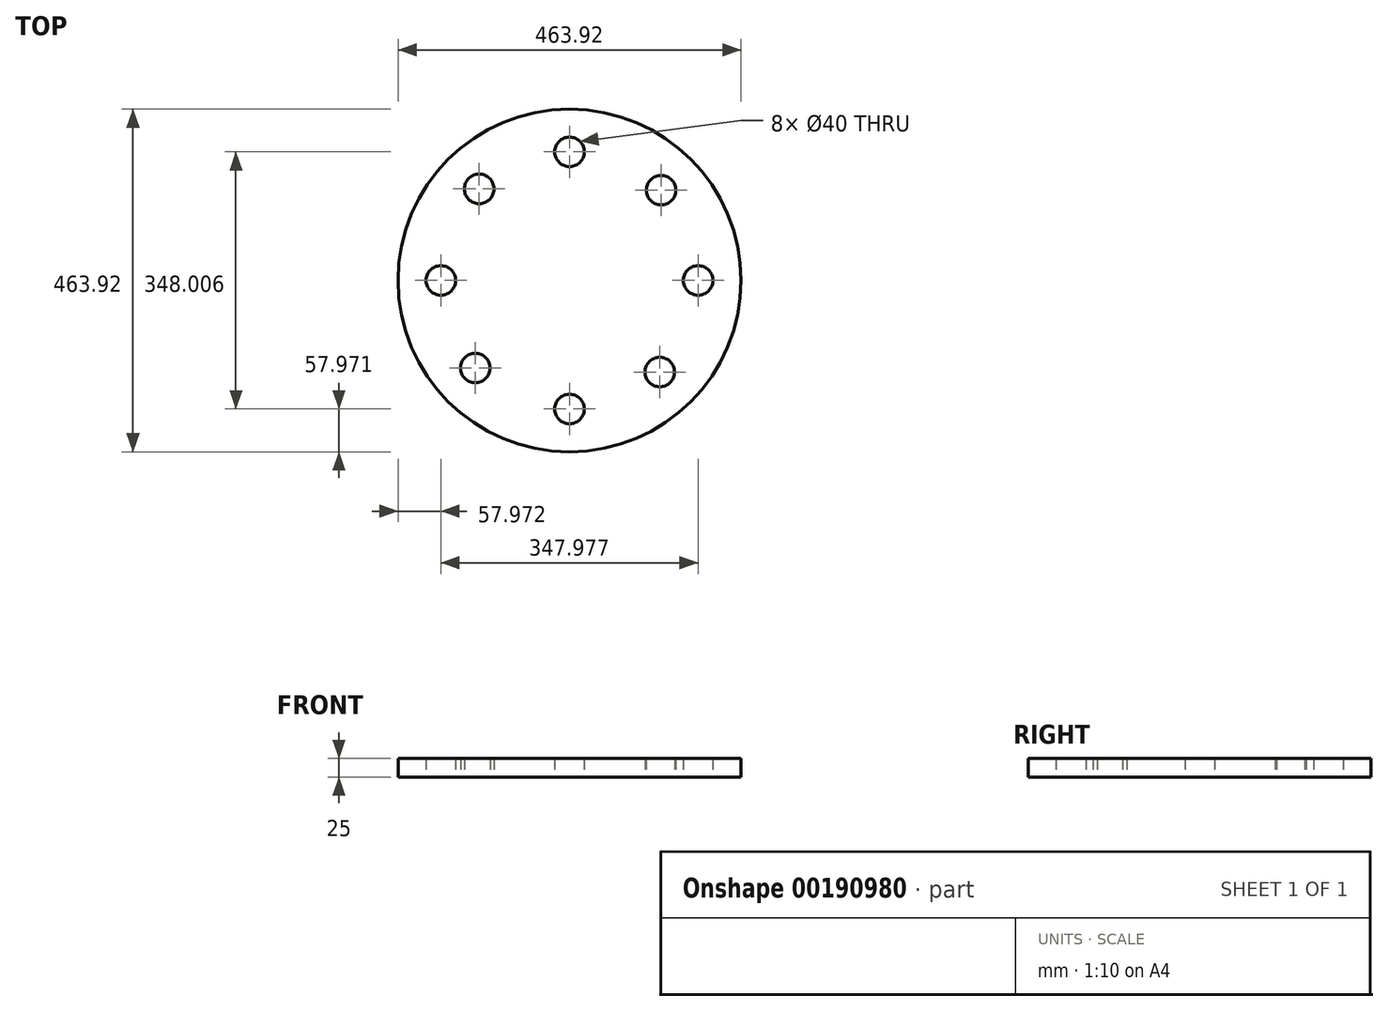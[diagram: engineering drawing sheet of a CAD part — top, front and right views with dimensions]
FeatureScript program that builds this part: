
annotation { "Feature Type Name" : "Feature", "Feature Type Description" : "" }
export const myFeature = defineFeature(function(context is Context, id is Id, definition is map)
    precondition{}
    {
        {
            var Q0;
            Q0=qCreatedBy(makeId("Front.planeOp"),FACE);
            var sketch = newSketch(context, id + "F0", { "sketchPlane" : qUnion([Q0])});
            skLineSegment(sketch, "E0", {"start": v(109.81, 208.07) * mm, "end": v(109.81, 208.07) * mm});
            skLineSegment(sketch, "E1", {"start": v(-26.47, -25) * mm, "end": v(109.81, -25) * mm});
            skLineSegment(sketch, "E2", {"start": v(109.81, -25) * mm, "end": v(109.81, 0) * mm});
            skLineSegment(sketch, "E3", {"start": v(109.81, 0) * mm, "end": v(0, 0) * mm});
            skPoint(sketch, "E4.orphan", {"position": v(8.02, 98.99) * mm});
            skPoint(sketch, "E5.start.orphan", {"position": v(-13.24, 0) * mm});
            skLineSegment(sketch, "E6", {"start": v(-191.48, 113.01) * mm, "end": v(-191.48, 113.01) * mm});
            skPoint(sketch, "E7", {"position": v(-12.02, 0) * mm});
            skPoint(sketch, "E8.start.orphan", {"position": v(16.05, 197.97) * mm});
            skPoint(sketch, "E9.start.orphan", {"position": v(109.81, 182.64) * mm});
            skLineSegment(sketch, "E10", {"start": v(-122.15, 113.01) * mm, "end": v(-122.15, 240.78) * mm});
            skLineSegment(sketch, "E11", {"start": v(109.81, 0) * mm, "end": v(-26.47, 0) * mm});
            skPoint(sketch, "E12.end.orphan", {"position": v(34.99, 113.01) * mm});
            skPoint(sketch, "E13.orphan", {"position": v(8.52, 113.01) * mm});
            skPoint(sketch, "E14.MirrorCS.start.orphan", {"position": v(0, 226.02) * mm});
            skPoint(sketch, "E15.MirrorCS.start.orphan", {"position": v(-26.47, 226.02) * mm});
            skPoint(sketch, "E16.MirrorCS.end.orphan", {"position": v(109.81, 226.02) * mm});
            skPoint(sketch, "E16.MirrorCS.start.orphan", {"position": v(109.81, 251.02) * mm});
            skPoint(sketch, "E17.MirrorCS.start.orphan", {"position": v(-26.47, 251.02) * mm});
            skPoint(sketch, "E18.end.orphan", {"position": v(-122.15, -30.7) * mm});
            skPoint(sketch, "E19.orphan", {"position": v(-165.01, 113.01) * mm});
            skPoint(sketch, "E20.end.orphan", {"position": v(-79.29, 113.01) * mm});
            skPoint(sketch, "E21.end.orphan", {"position": v(-10.43, 197.97) * mm});
            skPoint(sketch, "E21.start.orphan", {"position": v(-10.43, 208.07) * mm});
            skLineSegment(sketch, "E22", {"start": v(-26.47, -25) * mm, "end": v(-122.15, -25) * mm});
            skPoint(sketch, "E23.endSnap0", {"position": v(41.67, 0) * mm});
            skLineSegment(sketch, "E24", {"start": v(-122.15, 0) * mm, "end": v(-26.47, 0) * mm});
            skLineSegment(sketch, "E25", {"start": v(-122.15, 113.01) * mm, "end": v(-122.15, -25) * mm});
            skPoint(sketch, "E23.end.orphan", {"position": v(-166.52, 0) * mm});
            skSolve(sketch);
        }
        {
            var Q0;
            Q0=qSketchRegion(id+"F0",true);
            var Q1;
            Q1=sQuery(id+"F0.wireOp",EDGE,"E10");
            revolve(context, id + "F1", {"entities" : qUnion([Q0]), "axis" : qUnion([Q1]), "revolveType" : RevolveType.FULL});
        }
        {
            var Q0;
            Q0=makeQuery(id+"F1.opRevolve","SWEPT_FACE",FACE,{"disambiguationData":[OSD([sQuery(id+"F0.wireOp",EDGE,"E1")])]});
            var sketch = newSketch(context, id + "F2", { "sketchPlane" : qUnion([Q0])});
            skCircle(sketch, "E26", {"center": v(-249.62, 118.42) * mm, "radius": 20 * mm});
            skCircle(sketch, "E27", {"center": v(-296.14, 0) * mm, "radius": 20 * mm});
            skCircle(sketch, "E28", {"center": v(-244.3, -123.9) * mm, "radius": 20 * mm});
            skCircle(sketch, "E29", {"center": v(1.76, -122.14) * mm, "radius": 20 * mm});
            skCircle(sketch, "E30", {"center": v(51.84, 0) * mm, "radius": 20 * mm});
            skCircle(sketch, "E31", {"center": v(0, 123.9) * mm, "radius": 20 * mm});
            skCircle(sketch, "E32", {"center": v(-122.15, 173.99) * mm, "radius": 20 * mm});
            skLineSegment(sketch, "E33.trimOffspring", {"start": v(-122.15, 0) * mm, "end": v(-122.1, 153.99) * mm});
            skLineSegment(sketch, "E34.trimOffspring", {"start": v(-122.1, 0) * mm, "end": v(-122.15, 0.04) * mm});
            skLineSegment(sketch, "E35.trimOffspring", {"start": v(51.26, 0) * mm, "end": v(51.84, 0) * mm});
            skLineSegment(sketch, "E36.trimOffspring", {"start": v(71.84, 0) * mm, "end": v(71.9, 0) * mm});
            skCircle(sketch, "E37", {"center": v(-122.1, -174.02) * mm, "radius": 20 * mm});
            skArc(sketch, "E38", {"start": v(-244.3, -123.9) * mm, "mid": v(-122.1, -174.02) * mm, "end": v(0.08, -123.9) * mm});
            skLineSegment(sketch, "E39", {"start": v(-122.15, 0) * mm, "end": v(-122.1, -174.02) * mm});
            skLineSegment(sketch, "E40", {"start": v(-122.16, 31.14) * mm, "end": v(-122.1, 0.38) * mm});
            skCircle(sketch, "E41", {"center": v(-122.1, 0) * mm, "radius": 174.02 * mm, "construction": true});
            skSolve(sketch);
        }
        {
            var Q0;
            Q0=makeQuery(id+"F2.imprint","IMPRINT",FACE,{"disambiguationData":[TD([[makeQuery(id+"F2.imprint","IMPRINT",EDGE,{"derivedFrom":sQuery(id+"F2.wireOp",EDGE,"E27")}),1.0]])]});
            extrude(context, id + "F3", {"entities" : qUnion([Q0]), "operationType" : NewBodyOperationType.REMOVE, "oppositeDirection" : true, "depth" : 507.7 * mm});
        }
        {
            var Q0;
            Q0=qSketchRegion(id+"F2",true);
            extrude(context, id + "F4", {"entities" : qUnion([Q0]), "operationType" : NewBodyOperationType.REMOVE, "oppositeDirection" : true, "depth" : 346.47 * mm});
        }
    });
